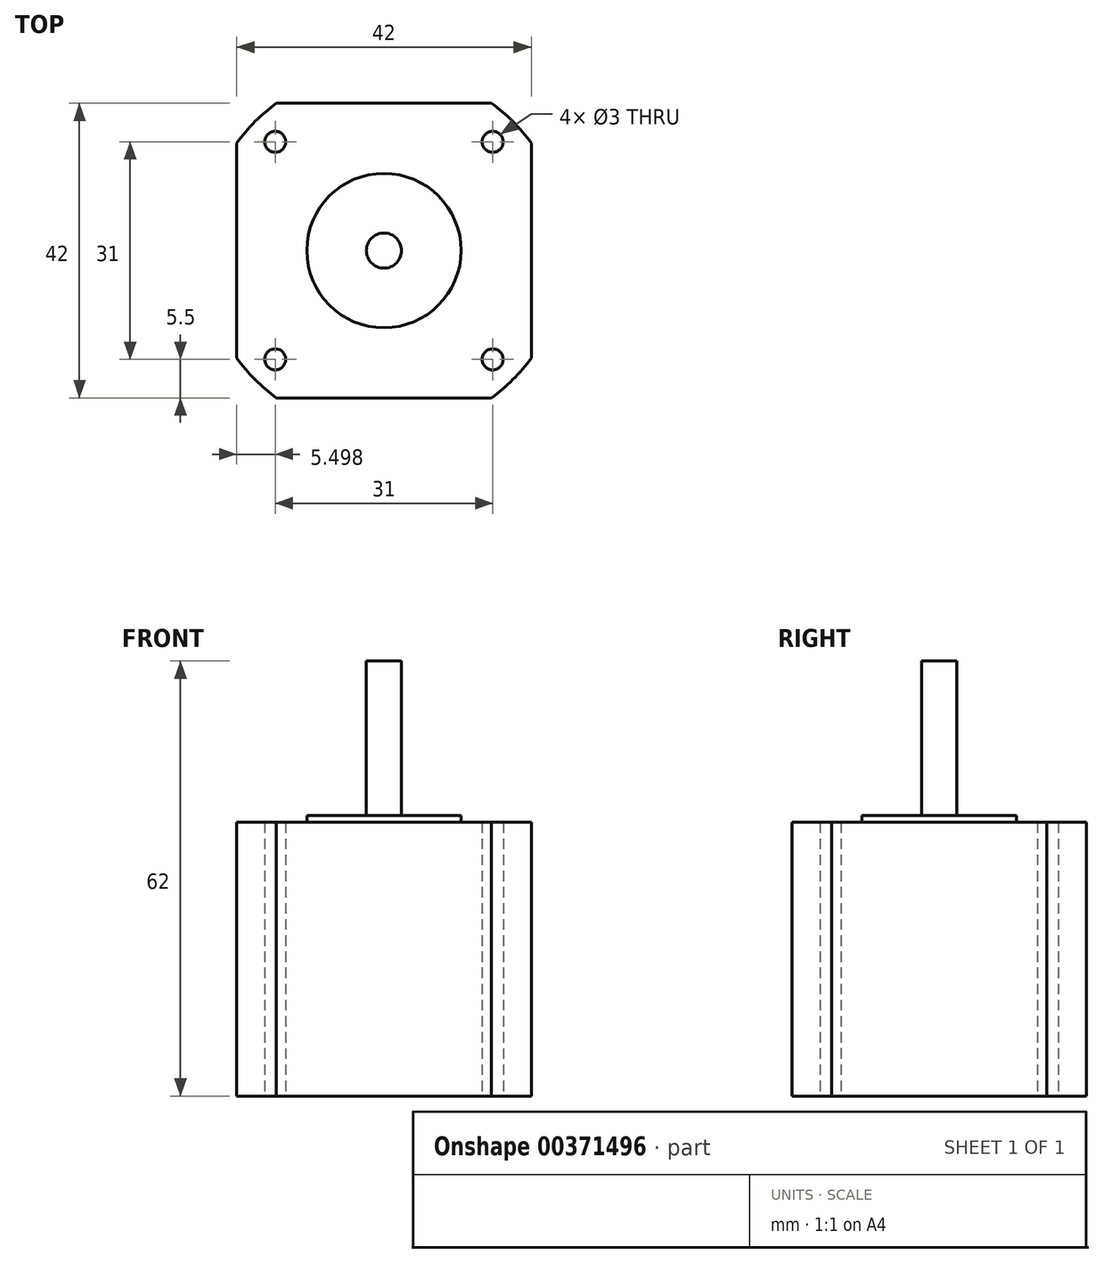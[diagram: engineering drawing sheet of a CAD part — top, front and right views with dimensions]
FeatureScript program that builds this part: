
annotation { "Feature Type Name" : "Feature", "Feature Type Description" : "" }
export const myFeature = defineFeature(function(context is Context, id is Id, definition is map)
    precondition{}
    {
        {
            var Q0;
            Q0=qCreatedBy(makeId("Top.planeOp"),FACE);
            var sketch = newSketch(context, id + "F0", { "sketchPlane" : qUnion([Q0])});
            skLineSegment(sketch, "E0.bottom", {"start": v(-61, -62.94) * mm, "end": v(-30.34, -62.94) * mm});
            skLineSegment(sketch, "E0.top", {"start": v(-61, -20.94) * mm, "end": v(-30.34, -20.94) * mm});
            skLineSegment(sketch, "E0.left", {"start": v(-66.67, -57.27) * mm, "end": v(-66.67, -26.61) * mm});
            skLineSegment(sketch, "E0.right", {"start": v(-24.67, -57.27) * mm, "end": v(-24.67, -26.61) * mm});
            skCircle(sketch, "E1", {"center": v(-61.17, -26.44) * mm, "radius": 1.5 * mm});
            skCircle(sketch, "E2", {"center": v(-30.17, -26.44) * mm, "radius": 1.5 * mm});
            skCircle(sketch, "E3", {"center": v(-30.17, -57.44) * mm, "radius": 1.5 * mm});
            skCircle(sketch, "E4", {"center": v(-61.17, -57.44) * mm, "radius": 1.5 * mm});
            skArc(sketch, "E5", {"start": v(-61, -20.94) * mm, "mid": v(-64.06, -23.56) * mm, "end": v(-66.67, -26.61) * mm});
            skPoint(sketch, "E5.centerSnap0", {"position": v(-45.67, -20.94) * mm});
            skPoint(sketch, "E5.centerSnap1", {"position": v(-24.67, -41.94) * mm});
            skPoint(sketch, "E6.orphan", {"position": v(-66.67, -20.94) * mm});
            skPoint(sketch, "E7.orphan", {"position": v(-24.67, -20.94) * mm});
            skArc(sketch, "E8.trimOffspring", {"start": v(-24.67, -26.61) * mm, "mid": v(-27.29, -23.56) * mm, "end": v(-30.34, -20.94) * mm});
            skPoint(sketch, "E9.orphan", {"position": v(-24.67, -62.94) * mm});
            skArc(sketch, "E10.trimOffspring", {"start": v(-30.34, -62.94) * mm, "mid": v(-27.29, -60.33) * mm, "end": v(-24.67, -57.27) * mm});
            skArc(sketch, "E11.trimOffspring", {"start": v(-66.67, -57.27) * mm, "mid": v(-64.06, -60.33) * mm, "end": v(-61, -62.94) * mm});
            skSolve(sketch);
        }
        {
            var Q0;
            Q0=makeQuery(id+"F0.imprint","IMPRINT",FACE,{"disambiguationData":[TD([[makeQuery(id+"F0.imprint","IMPRINT",EDGE,{"derivedFrom":sQuery(id+"F0.wireOp",EDGE,"E0.bottom")}),1.0]])]});
            extrude(context, id + "F1", {"entities" : qUnion([Q0]), "depth" : 39 * mm});
        }
        {
            var Q0;
            Q0=makeQuery(id+"F1.opExtrude","CAP_FACE",FACE,{"disambiguationData":[OSD([sQuery(id+"F0.wireOp",EDGE,"E0.bottom"),sQuery(id+"F0.wireOp",EDGE,"E0.top"),sQuery(id+"F0.wireOp",EDGE,"E0.left"),sQuery(id+"F0.wireOp",EDGE,"E0.right"),sQuery(id+"F0.wireOp",EDGE,"E1"),sQuery(id+"F0.wireOp",EDGE,"E2"),sQuery(id+"F0.wireOp",EDGE,"E3"),sQuery(id+"F0.wireOp",EDGE,"E4"),sQuery(id+"F0.wireOp",EDGE,"E5"),sQuery(id+"F0.wireOp",EDGE,"E8.trimOffspring"),sQuery(id+"F0.wireOp",EDGE,"E10.trimOffspring"),sQuery(id+"F0.wireOp",EDGE,"E11.trimOffspring")])],"isStart":false});
            var sketch = newSketch(context, id + "F2", { "sketchPlane" : qUnion([Q0])});
            skCircle(sketch, "E12", {"center": v(-45.67, -41.94) * mm, "radius": 2.5 * mm});
            skSolve(sketch);
        }
        {
            var Q0;
            Q0=makeQuery(id+"F2.imprint","IMPRINT",FACE,{"disambiguationData":[TD([[makeQuery(id+"F2.imprint","IMPRINT",EDGE,{"derivedFrom":sQuery(id+"F2.wireOp",EDGE,"E12")}),1.0]])]});
            extrude(context, id + "F3", {"entities" : qUnion([Q0]), "operationType" : NewBodyOperationType.ADD, "depth" : 23 * mm});
        }
        {
            var Q0;
            Q0=makeQuery(id+"F1.opExtrude","CAP_FACE",FACE,{"disambiguationData":[OSD([sQuery(id+"F0.wireOp",EDGE,"E0.bottom"),sQuery(id+"F0.wireOp",EDGE,"E0.top"),sQuery(id+"F0.wireOp",EDGE,"E0.left"),sQuery(id+"F0.wireOp",EDGE,"E0.right"),sQuery(id+"F0.wireOp",EDGE,"E1"),sQuery(id+"F0.wireOp",EDGE,"E2"),sQuery(id+"F0.wireOp",EDGE,"E3"),sQuery(id+"F0.wireOp",EDGE,"E4"),sQuery(id+"F0.wireOp",EDGE,"E5"),sQuery(id+"F0.wireOp",EDGE,"E8.trimOffspring"),sQuery(id+"F0.wireOp",EDGE,"E10.trimOffspring"),sQuery(id+"F0.wireOp",EDGE,"E11.trimOffspring")])],"isStart":false});
            var sketch = newSketch(context, id + "F4", { "sketchPlane" : qUnion([Q0])});
            skCircle(sketch, "E13", {"center": v(-45.67, -41.94) * mm, "radius": 11 * mm});
            skSolve(sketch);
        }
        {
            var Q0;
            Q0=makeQuery(id+"F4.imprint","IMPRINT",FACE,{"disambiguationData":[TD([[makeQuery(id+"F4.imprint","IMPRINT",EDGE,{"derivedFrom":sQuery(id+"F4.wireOp",EDGE,"E13")}),1.0]])]});
            extrude(context, id + "F5", {"entities" : qUnion([Q0]), "operationType" : NewBodyOperationType.ADD, "depth" : 1 * mm});
        }
    });
